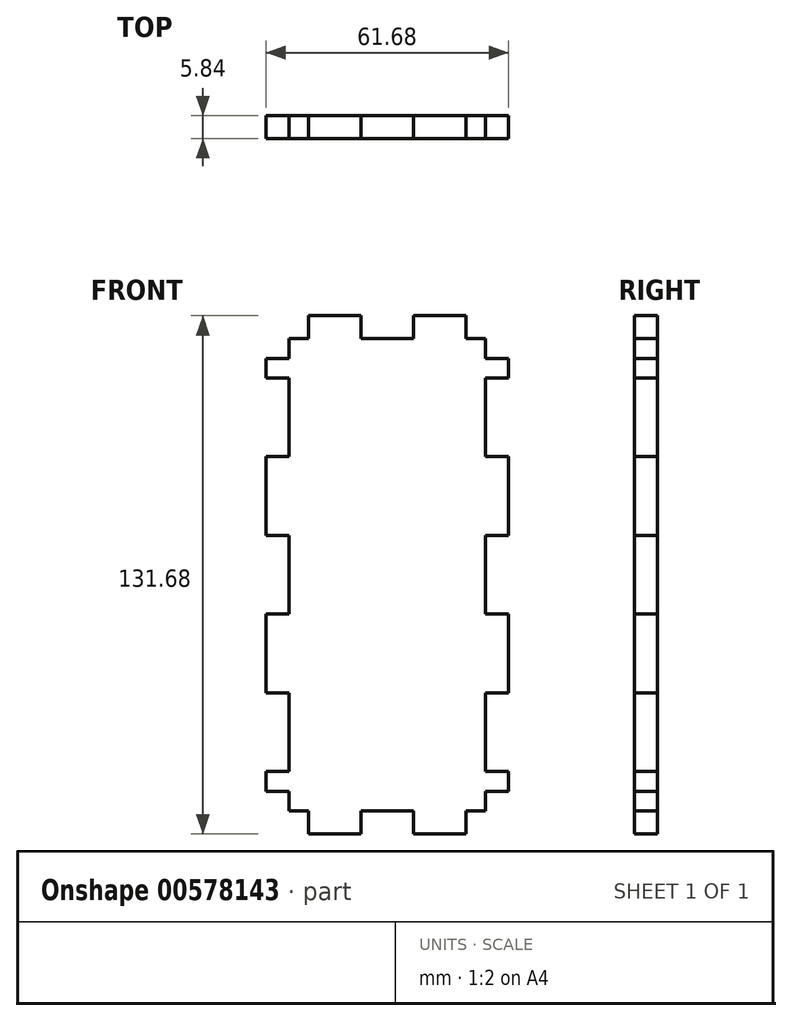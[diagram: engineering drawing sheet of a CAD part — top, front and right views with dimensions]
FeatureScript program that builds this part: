
annotation { "Feature Type Name" : "Feature", "Feature Type Description" : "" }
export const myFeature = defineFeature(function(context is Context, id is Id, definition is map)
    precondition{}
    {
        {
            var Q0;
            Q0=qCreatedBy(makeId("Front.planeOp"),FACE);
            var sketch = newSketch(context, id + "F0", { "sketchPlane" : qUnion([Q0])});
            skLineSegment(sketch, "E0.bottom", {"start": v(-25, 60) * mm, "end": v(25, 60) * mm});
            skLineSegment(sketch, "E0.top", {"start": v(-25, -60) * mm, "end": v(25, -60) * mm});
            skLineSegment(sketch, "E0.left", {"start": v(-25, 60) * mm, "end": v(-25, -60) * mm});
            skLineSegment(sketch, "E0.right", {"start": v(25, 60) * mm, "end": v(25, -60) * mm});
            skLineSegment(sketch, "E1.left", {"start": v(30.84, 55) * mm, "end": v(30.84, 50) * mm});
            skLineSegment(sketch, "E1.right", {"start": v(-30.84, 55) * mm, "end": v(-30.84, 50) * mm});
            skPoint(sketch, "E1.middle", {"position": v(0, 0) * mm});
            skLineSegment(sketch, "E2.left", {"start": v(6.67, -65.84) * mm, "end": v(6.67, -60) * mm});
            skLineSegment(sketch, "E2.right", {"start": v(-6.67, -65.84) * mm, "end": v(-6.67, -60) * mm});
            skPoint(sketch, "E2.middle", {"position": v(0, -60) * mm});
            skPoint(sketch, "E3.middle", {"position": v(-25, -60) * mm});
            skLineSegment(sketch, "E4.left", {"start": v(-6.67, 65.84) * mm, "end": v(-6.67, 60) * mm});
            skLineSegment(sketch, "E4.right", {"start": v(6.67, 65.84) * mm, "end": v(6.67, 60) * mm});
            skPoint(sketch, "E4.middle", {"position": v(0, 60) * mm});
            skPoint(sketch, "E5.middle", {"position": v(-25, 60) * mm});
            skPoint(sketch, "E6.middle", {"position": v(25, 60) * mm});
            skLineSegment(sketch, "E7.bottom", {"start": v(-6.67, 60) * mm, "end": v(-20, 60) * mm});
            skLineSegment(sketch, "E7.left", {"start": v(-6.67, 60) * mm, "end": v(-6.67, 65.84) * mm});
            skLineSegment(sketch, "E7.right", {"start": v(-20, 60) * mm, "end": v(-20, 65.84) * mm});
            skLineSegment(sketch, "E8.bottom", {"start": v(6.67, 60) * mm, "end": v(20, 60) * mm});
            skLineSegment(sketch, "E8.left", {"start": v(6.67, 60) * mm, "end": v(6.67, 65.84) * mm});
            skLineSegment(sketch, "E8.right", {"start": v(20, 60) * mm, "end": v(20, 65.84) * mm});
            skLineSegment(sketch, "E9.bottom", {"start": v(-6.67, -60) * mm, "end": v(-20, -60) * mm});
            skLineSegment(sketch, "E9.left", {"start": v(-6.67, -60) * mm, "end": v(-6.67, -65.84) * mm});
            skLineSegment(sketch, "E9.right", {"start": v(-20, -60) * mm, "end": v(-20, -65.84) * mm});
            skLineSegment(sketch, "E10.bottom", {"start": v(6.67, -60) * mm, "end": v(20, -60) * mm});
            skLineSegment(sketch, "E10.left", {"start": v(6.67, -60) * mm, "end": v(6.67, -65.84) * mm});
            skLineSegment(sketch, "E10.right", {"start": v(20, -60) * mm, "end": v(20, -65.84) * mm});
            skPoint(sketch, "E11.orphan", {"position": v(-6.67, 54.16) * mm});
            skPoint(sketch, "E12.orphan", {"position": v(6.67, 54.16) * mm});
            skPoint(sketch, "E13.orphan", {"position": v(-6.67, -54.16) * mm});
            skPoint(sketch, "E14.orphan", {"position": v(6.67, -54.16) * mm});
            skLineSegment(sketch, "E15.bottom", {"start": v(-25, 10) * mm, "end": v(-30.84, 10) * mm});
            skLineSegment(sketch, "E15.top", {"start": v(-25, -10) * mm, "end": v(-30.84, -10) * mm});
            skLineSegment(sketch, "E15.left", {"start": v(-25, 10) * mm, "end": v(-25, -10) * mm});
            skPoint(sketch, "E15.middle", {"position": v(-30.84, 0) * mm});
            skLineSegment(sketch, "E16.bottom", {"start": v(-30.84, 10) * mm, "end": v(-25, 10) * mm});
            skLineSegment(sketch, "E16.top", {"start": v(-30.84, 30) * mm, "end": v(-25, 30) * mm});
            skLineSegment(sketch, "E16.right", {"start": v(-25, 10) * mm, "end": v(-25, 30) * mm});
            skPoint(sketch, "E16.middle", {"position": v(-30.84, 20) * mm});
            skLineSegment(sketch, "E17.bottom", {"start": v(-30.84, -10) * mm, "end": v(-25, -10) * mm});
            skLineSegment(sketch, "E17.top", {"start": v(-30.84, -30) * mm, "end": v(-25, -30) * mm});
            skLineSegment(sketch, "E17.right", {"start": v(-25, -10) * mm, "end": v(-25, -30) * mm});
            skPoint(sketch, "E17.middle", {"position": v(-30.84, -20) * mm});
            skLineSegment(sketch, "E18.top", {"start": v(-30.84, 50) * mm, "end": v(-25, 50) * mm});
            skLineSegment(sketch, "E18.right", {"start": v(-25, 30) * mm, "end": v(-25, 50) * mm});
            skPoint(sketch, "E18.middle", {"position": v(-30.84, 40) * mm});
            skPoint(sketch, "E19.cornerSnap0", {"position": v(-36.68, 20) * mm});
            skLineSegment(sketch, "E20.top", {"start": v(-30.84, -50) * mm, "end": v(-25, -50) * mm});
            skLineSegment(sketch, "E20.right", {"start": v(-25, -30) * mm, "end": v(-25, -50) * mm});
            skPoint(sketch, "E20.middle", {"position": v(-30.84, -40) * mm});
            skLineSegment(sketch, "E21.bottom", {"start": v(-25, 55) * mm, "end": v(-30.84, 55) * mm});
            skLineSegment(sketch, "E21.top", {"start": v(-25, 50) * mm, "end": v(-30.84, 50) * mm});
            skLineSegment(sketch, "E21.left", {"start": v(-25, 55) * mm, "end": v(-25, 50) * mm});
            skLineSegment(sketch, "E22.bottom", {"start": v(-25, -50) * mm, "end": v(-30.84, -50) * mm});
            skLineSegment(sketch, "E22.top", {"start": v(-25, -55) * mm, "end": v(-30.84, -55) * mm});
            skLineSegment(sketch, "E22.left", {"start": v(-25, -50) * mm, "end": v(-25, -55) * mm});
            skLineSegment(sketch, "E23.bottom", {"start": v(25, 10) * mm, "end": v(30.84, 10) * mm});
            skLineSegment(sketch, "E23.top", {"start": v(25, -10) * mm, "end": v(30.84, -10) * mm});
            skLineSegment(sketch, "E23.left", {"start": v(25, 10) * mm, "end": v(25, -10) * mm});
            skPoint(sketch, "E23.middle", {"position": v(30.84, 0) * mm});
            skLineSegment(sketch, "E24.bottom", {"start": v(30.84, 10) * mm, "end": v(25, 10) * mm});
            skLineSegment(sketch, "E24.top", {"start": v(30.84, 30) * mm, "end": v(25, 30) * mm});
            skLineSegment(sketch, "E24.right", {"start": v(25, 10) * mm, "end": v(25, 30) * mm});
            skPoint(sketch, "E24.middle", {"position": v(30.84, 20) * mm});
            skLineSegment(sketch, "E25.bottom", {"start": v(30.84, -10) * mm, "end": v(25, -10) * mm});
            skLineSegment(sketch, "E25.top", {"start": v(30.84, -30) * mm, "end": v(25, -30) * mm});
            skLineSegment(sketch, "E25.right", {"start": v(25, -10) * mm, "end": v(25, -30) * mm});
            skPoint(sketch, "E25.middle", {"position": v(30.84, -20) * mm});
            skLineSegment(sketch, "E26.top", {"start": v(30.84, 50) * mm, "end": v(25, 50) * mm});
            skLineSegment(sketch, "E26.right", {"start": v(25, 30) * mm, "end": v(25, 50) * mm});
            skPoint(sketch, "E26.middle", {"position": v(30.84, 40) * mm});
            skLineSegment(sketch, "E27.top", {"start": v(30.84, -50) * mm, "end": v(25, -50) * mm});
            skLineSegment(sketch, "E27.right", {"start": v(25, -30) * mm, "end": v(25, -50) * mm});
            skPoint(sketch, "E27.middle", {"position": v(30.84, -40) * mm});
            skLineSegment(sketch, "E28.bottom", {"start": v(25, -50) * mm, "end": v(30.84, -50) * mm});
            skLineSegment(sketch, "E28.top", {"start": v(25, -55) * mm, "end": v(30.84, -55) * mm});
            skLineSegment(sketch, "E28.left", {"start": v(25, -50) * mm, "end": v(25, -55) * mm});
            skLineSegment(sketch, "E29.bottom", {"start": v(25, 55) * mm, "end": v(30.84, 55) * mm});
            skLineSegment(sketch, "E29.top", {"start": v(25, 50) * mm, "end": v(30.84, 50) * mm});
            skLineSegment(sketch, "E29.left", {"start": v(25, 55) * mm, "end": v(25, 50) * mm});
            skPoint(sketch, "E30.orphan", {"position": v(-36.68, 50) * mm});
            skPoint(sketch, "E31.orphan", {"position": v(-36.68, 30) * mm});
            skPoint(sketch, "E32.orphan", {"position": v(-36.68, 10) * mm});
            skPoint(sketch, "E33.orphan", {"position": v(-36.68, -10) * mm});
            skPoint(sketch, "E34.orphan", {"position": v(-36.68, -30) * mm});
            skPoint(sketch, "E22.right.end.orphan", {"position": v(-36.68, -55) * mm});
            skPoint(sketch, "E35.orphan", {"position": v(-36.68, -50) * mm});
            skPoint(sketch, "E36.orphan", {"position": v(36.68, 10) * mm});
            skPoint(sketch, "E37.orphan", {"position": v(36.68, -10) * mm});
            skPoint(sketch, "E38.orphan", {"position": v(36.68, -30) * mm});
            skPoint(sketch, "E39.orphan", {"position": v(36.68, -50) * mm});
            skPoint(sketch, "E40.orphan", {"position": v(36.68, -55) * mm});
            skPoint(sketch, "E41.orphan", {"position": v(36.68, 50) * mm});
            skPoint(sketch, "E42.orphan", {"position": v(36.68, 30) * mm});
            skLineSegment(sketch, "E43.bottom", {"start": v(-20, 60) * mm, "end": v(-6.67, 60) * mm});
            skLineSegment(sketch, "E43.top", {"start": v(-20, 65.84) * mm, "end": v(-6.67, 65.84) * mm});
            skLineSegment(sketch, "E44.top", {"start": v(6.67, 65.84) * mm, "end": v(20, 65.84) * mm});
            skLineSegment(sketch, "E45.top", {"start": v(-6.67, -65.84) * mm, "end": v(-20, -65.84) * mm});
            skLineSegment(sketch, "E46.top", {"start": v(6.67, -65.84) * mm, "end": v(20, -65.84) * mm});
            skPoint(sketch, "E47.orphan", {"position": v(30.84, 65.84) * mm});
            skPoint(sketch, "E48.orphan", {"position": v(-30.84, 65.84) * mm});
            skLineSegment(sketch, "E49.trimOffspring", {"start": v(-30.84, 30) * mm, "end": v(-30.84, 10) * mm});
            skLineSegment(sketch, "E50.trimOffspring", {"start": v(-30.84, -10) * mm, "end": v(-30.84, -30) * mm});
            skLineSegment(sketch, "E51.trimOffspring", {"start": v(-30.84, -40) * mm, "end": v(-30.84, -55) * mm});
            skPoint(sketch, "E52.trimOffspring.end.orphan", {"position": v(-30.84, -65.84) * mm});
            skPoint(sketch, "E53.orphan", {"position": v(30.84, -65.84) * mm});
            skLineSegment(sketch, "E54.trimOffspring", {"start": v(30.84, -50) * mm, "end": v(30.84, -55) * mm});
            skLineSegment(sketch, "E55.trimOffspring", {"start": v(30.84, -10) * mm, "end": v(30.84, -30) * mm});
            skLineSegment(sketch, "E56.trimOffspring", {"start": v(30.84, 30) * mm, "end": v(30.84, 10) * mm});
            skSolve(sketch);
        }
        {
            var Q0;
            Q0=qSketchRegion(id+"F0",true);
            extrude(context, id + "F1", {"entities" : qUnion([Q0]), "depth" : 5.84 * mm, "offsetDistance" : 25 * mm});
        }
    });
